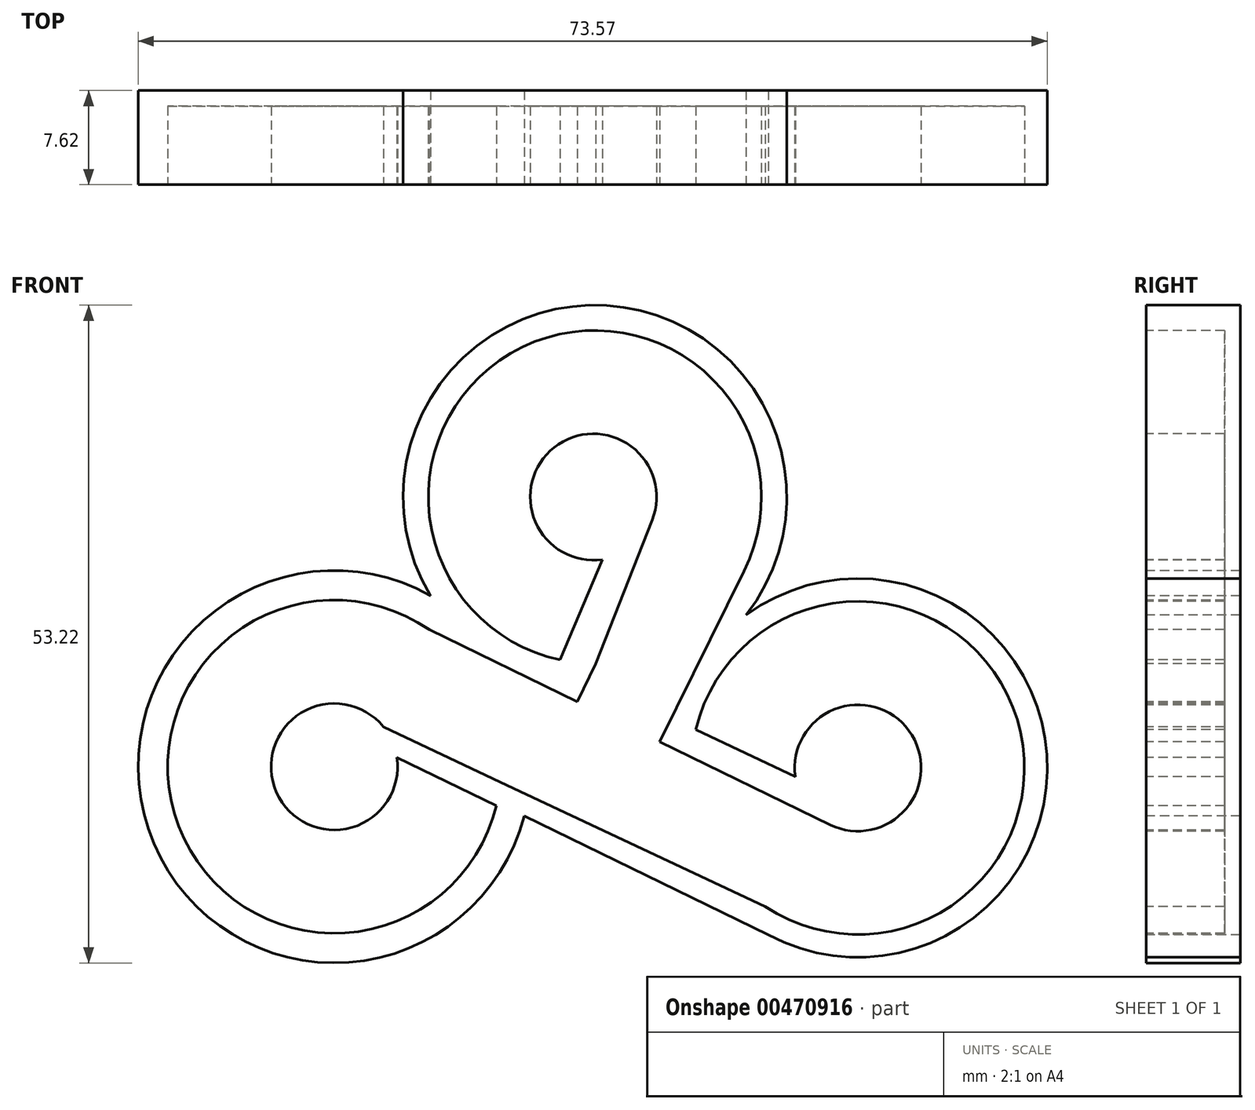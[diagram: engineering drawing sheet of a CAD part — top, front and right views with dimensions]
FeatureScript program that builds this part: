
annotation { "Feature Type Name" : "Feature", "Feature Type Description" : "" }
export const myFeature = defineFeature(function(context is Context, id is Id, definition is map)
    precondition{}
    {
        {
            var Q0;
            Q0=qCreatedBy(makeId("Front.planeOp"),FACE);
            var sketch = newSketch(context, id + "F0", { "sketchPlane" : qUnion([Q0])});
            skLineSegment(sketch, "E0.bottom", {"start": v(-36.13, 19.52) * mm, "end": v(40.07, 19.52) * mm});
            skLineSegment(sketch, "E0.top", {"start": v(-36.13, -56.68) * mm, "end": v(40.07, -56.68) * mm});
            skLineSegment(sketch, "E0.left", {"start": v(-36.13, 19.52) * mm, "end": v(-36.13, -56.68) * mm});
            skLineSegment(sketch, "E0.right", {"start": v(40.07, 19.52) * mm, "end": v(40.07, -56.68) * mm});
            skSolve(sketch);
        }
        {
            var Q0;
            Q0=makeQuery(id+"F0.imprint","IMPRINT",FACE,{"disambiguationData":[TD([[makeQuery(id+"F0.imprint","IMPRINT",EDGE,{"derivedFrom":sQuery(id+"F0.wireOp",EDGE,"E0.bottom")}),-1.0]])]});
            extrude(context, id + "F1", {"entities" : qUnion([Q0]), "depth" : 7.62 * mm});
        }
        {
            var Q0;
            Q0=makeQuery(id+"F1.opExtrude","CAP_FACE",FACE,{"disambiguationData":[OSD([sQuery(id+"F0.wireOp",EDGE,"E0.bottom"),sQuery(id+"F0.wireOp",EDGE,"E0.top"),sQuery(id+"F0.wireOp",EDGE,"E0.left"),sQuery(id+"F0.wireOp",EDGE,"E0.right")])],"isStart":false});
            var sketch = newSketch(context, id + "F2", { "sketchPlane" : qUnion([Q0])});
            skArc(sketch, "E1", {"start": v(-14.97, -27.72) * mm, "mid": v(-23.61, -33.02) * mm, "end": v(-13.87, -30.2) * mm});
            skArc(sketch, "E2", {"start": v(6.8, -11) * mm, "mid": v(-1.13, -5.11) * mm, "end": v(2.75, -14.2) * mm});
            skArc(sketch, "E3", {"start": v(21.2, -35.65) * mm, "mid": v(27.57, -28.04) * mm, "end": v(18.37, -31.76) * mm});
            skArc(sketch, "E4", {"start": v(-11.25, -19.87) * mm, "mid": v(-31.53, -35.75) * mm, "end": v(-5.83, -34.11) * mm});
            skArc(sketch, "E5", {"start": v(14.23, -15.11) * mm, "mid": v(-3.7, 3) * mm, "end": v(-0.67, -22.3) * mm});
            skArc(sketch, "E6", {"start": v(15.95, -42.26) * mm, "mid": v(35.98, -26.13) * mm, "end": v(10.32, -27.94) * mm});
            skLineSegment(sketch, "E7", {"start": v(-0.67, -22.3) * mm, "end": v(2.75, -14.2) * mm});
            skLineSegment(sketch, "E8", {"start": v(6.8, -11) * mm, "end": v(2.21, -22.6) * mm});
            skLineSegment(sketch, "E9", {"start": v(10.32, -27.94) * mm, "end": v(18.37, -31.76) * mm});
            skLineSegment(sketch, "E10", {"start": v(9.99, -30.2) * mm, "end": v(21.2, -35.65) * mm});
            skLineSegment(sketch, "E11", {"start": v(9.99, -30.2) * mm, "end": v(7.38, -28.93) * mm});
            skLineSegment(sketch, "E12", {"start": v(2.21, -22.6) * mm, "end": v(0.71, -25.69) * mm});
            skLineSegment(sketch, "E13", {"start": v(7.38, -28.93) * mm, "end": v(14.23, -15.11) * mm});
            skLineSegment(sketch, "E14", {"start": v(-5.5, -32.21) * mm, "end": v(-14.97, -27.72) * mm});
            skLineSegment(sketch, "E15", {"start": v(-13.87, -30.2) * mm, "end": v(-5.83, -34.11) * mm});
            skLineSegment(sketch, "E16", {"start": v(-5.5, -32.21) * mm, "end": v(15.95, -42.26) * mm});
            skLineSegment(sketch, "E17.trimOffspring", {"start": v(0.71, -25.69) * mm, "end": v(-11.25, -19.87) * mm});
            skSolve(sketch);
        }
        {
            var Q0;
            Q0=makeQuery(id+"F2.imprint","IMPRINT",FACE,{"disambiguationData":[TD([[makeQuery(id+"F2.imprint","IMPRINT",EDGE,{"derivedFrom":sQuery(id+"F2.wireOp",EDGE,"E1")}),-1.0]])]});
            extrude(context, id + "F3", {"entities" : qUnion([Q0]), "operationType" : NewBodyOperationType.REMOVE, "oppositeDirection" : true, "depth" : 6.35 * mm});
        }
        {
            var Q0;
            Q0=makeQuery(id+"F1.opExtrude","CAP_FACE",FACE,{"disambiguationData":[OSD([sQuery(id+"F0.wireOp",EDGE,"E0.bottom"),sQuery(id+"F0.wireOp",EDGE,"E0.top"),sQuery(id+"F0.wireOp",EDGE,"E0.left"),sQuery(id+"F0.wireOp",EDGE,"E0.right")])],"isStart":false});
            var sketch = newSketch(context, id + "F4", { "sketchPlane" : qUnion([Q0])});
            skArc(sketch, "E18", {"start": v(14.4, -18.68) * mm, "mid": v(3.1, 6.37) * mm, "end": v(-11.16, -17.1) * mm});
            skArc(sketch, "E19", {"start": v(16.19, -44.56) * mm, "mid": v(38.72, -29.99) * mm, "end": v(14.4, -18.68) * mm});
            skArc(sketch, "E20", {"start": v(-11.16, -17.1) * mm, "mid": v(-33.54, -37.17) * mm, "end": v(-3.57, -34.95) * mm});
            skLineSegment(sketch, "E21", {"start": v(16.19, -44.56) * mm, "end": v(-3.57, -34.95) * mm});
            skSolve(sketch);
        }
        {
            var Q0;
            Q0=makeQuery(id+"F4.imprint","IMPRINT",FACE,{"disambiguationData":[TD([[makeQuery(id+"F4.imprint","IMPRINT",EDGE,{"derivedFrom":sQuery(id+"F4.wireOp",EDGE,"E18")}),-1.0]])]});
            extrude(context, id + "F5", {"entities" : qUnion([Q0]), "operationType" : NewBodyOperationType.REMOVE, "oppositeDirection" : true, "depth" : 25.4 * mm});
        }
    });
